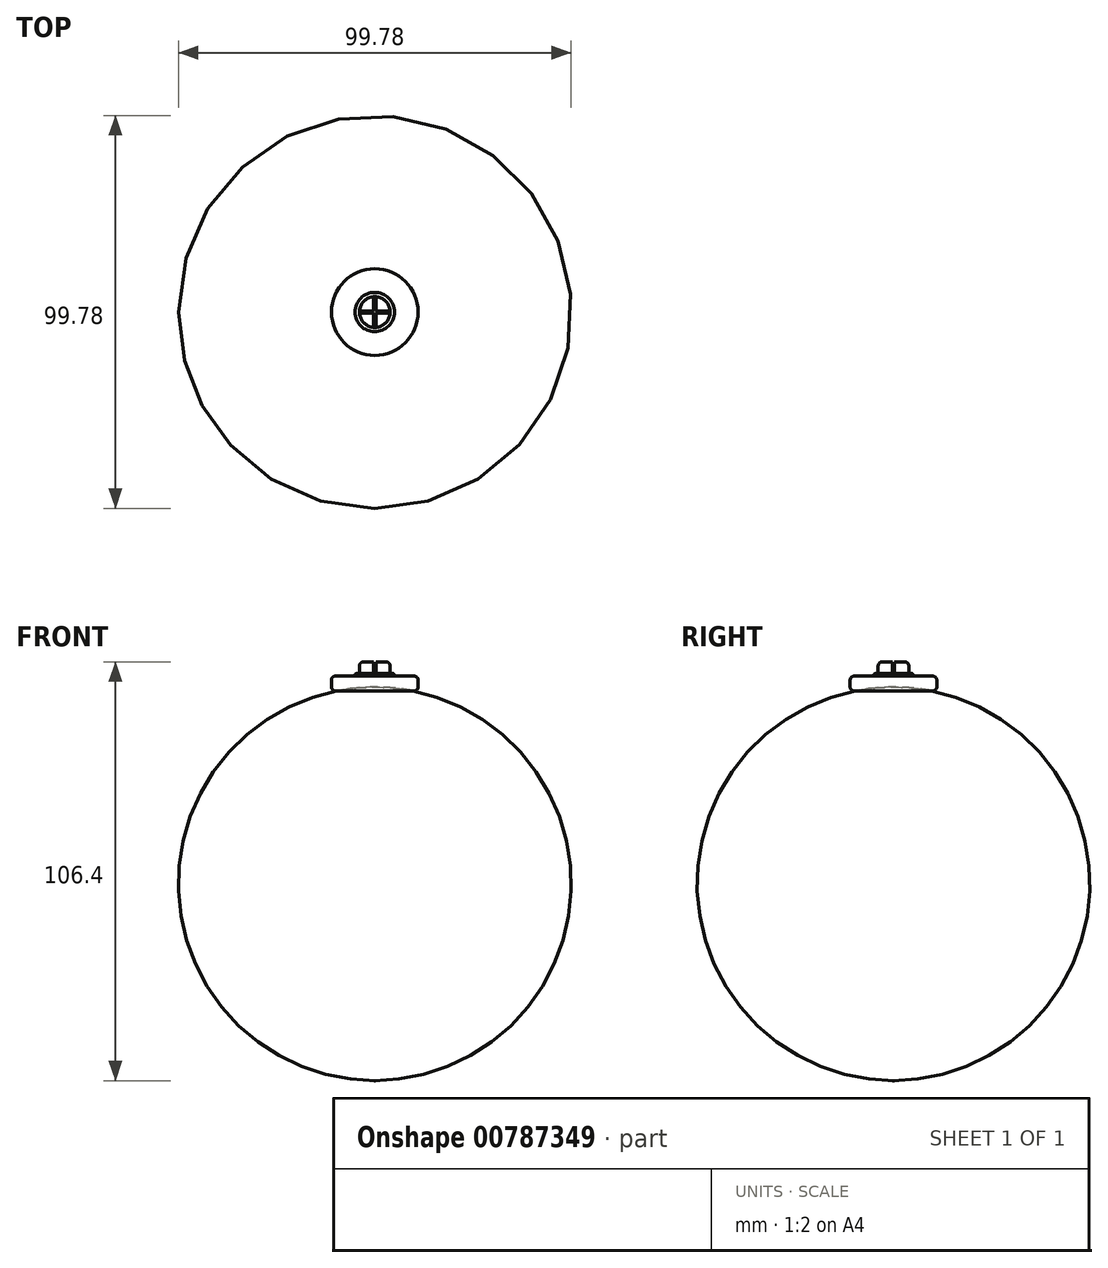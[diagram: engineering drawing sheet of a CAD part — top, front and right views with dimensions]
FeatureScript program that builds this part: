
annotation { "Feature Type Name" : "Feature", "Feature Type Description" : "" }
export const myFeature = defineFeature(function(context is Context, id is Id, definition is map)
    precondition{}
    {
        {
            var Q0;
            Q0=qCreatedBy(makeId("Front.planeOp"),FACE);
            var sketch = newSketch(context, id + "F0", { "sketchPlane" : qUnion([Q0])});
            skLineSegment(sketch, "E0", {"start": v(-11, 0) * mm, "end": v(-11, 4) * mm});
            skLineSegment(sketch, "E1", {"start": v(-11, 4) * mm, "end": v(0, 4) * mm});
            skArc(sketch, "E2", {"start": v(0, 1.2) * mm, "mid": v(-5.53, 0.9) * mm, "end": v(-11, 0) * mm});
            skLineSegment(sketch, "E3", {"start": v(0, 4) * mm, "end": v(0, 1.2) * mm});
            skLineSegment(sketch, "E4", {"start": v(-3.9, 4.6) * mm, "end": v(0, 4.6) * mm});
            skLineSegment(sketch, "E5", {"start": v(0, 4.6) * mm, "end": v(0, 4) * mm});
            skLineSegment(sketch, "E6", {"start": v(-3.9, 4.6) * mm, "end": v(-3.9, 7.6) * mm});
            skLineSegment(sketch, "E7", {"start": v(-3.9, 7.6) * mm, "end": v(0, 7.6) * mm});
            skLineSegment(sketch, "E8", {"start": v(0, 7.6) * mm, "end": v(0, 4.6) * mm});
            skLineSegment(sketch, "E9", {"start": v(-3.9, 4.6) * mm, "end": v(-5, 4.6) * mm});
            skLineSegment(sketch, "E10", {"start": v(-5, 4.6) * mm, "end": v(-5, 4) * mm});
            skSolve(sketch);
        }
        {
            var Q0;
            {var subQ2=sQuery(id+"F0.wireOp",EDGE,"Kpe3LUCm-XfSO-ckMI-Tb2P-7CUM5thwnmXW");Q0=makeQuery(id+"F0.imprint","IMPRINT",FACE,{"disambiguationData":[TD([[makeQuery(id+"F0.imprint","IMPRINT",EDGE,{"derivedFrom":subQ2}),-1.0]])]});}
            var Q1;
            Q1=makeQuery(id+"F0.imprint","IMPRINT",FACE,{"disambiguationData":[TD([[makeQuery(id+"F0.imprint","IMPRINT",EDGE,{"derivedFrom":sQuery(id+"F0.wireOp",EDGE,"E4")}),1.0]])]});
            var Q2;
            {var subQ3=sQuery(id+"F0.wireOp",EDGE,"E0");Q2=makeQuery(id+"F0.imprint","IMPRINT",FACE,{"disambiguationData":[TD([[makeQuery(id+"F0.imprint","IMPRINT",EDGE,{"derivedFrom":subQ3}),-1.0]])]});}
            var Q3;
            Q3=makeQuery(id+"F0.imprint","IMPRINT",FACE,{"disambiguationData":[TD([[makeQuery(id+"F0.imprint","IMPRINT",EDGE,{"derivedFrom":sQuery(id+"F0.wireOp",EDGE,"E4")}),-1.0]])]});
            var Q4;
            Q4=sQuery(id+"F0.wireOp",EDGE,"E8");
            revolve(context, id + "F1", {"surfaceOperationType" : NewSurfaceOperationType.NEW, "entities" : qUnion([Q0, Q1, Q2, Q3]), "axis" : qUnion([Q4]), "revolveType" : RevolveType.FULL});
        }
        {
            var Q0;
            Q0=makeQuery(id+"F1.opRevolve","SWEPT_FACE",FACE,{"disambiguationData":[OSD([sQuery(id+"F0.wireOp",EDGE,"E7")])]});
            var sketch = newSketch(context, id + "F2", { "sketchPlane" : qUnion([Q0])});
            skLineSegment(sketch, "E11", {"start": v(-0.3, 3.89) * mm, "end": v(-0.3, 0.3) * mm});
            skLineSegment(sketch, "E12", {"start": v(-0.3, 0.3) * mm, "end": v(-3.89, 0.3) * mm});
            skLineSegment(sketch, "E13.MirrorCS", {"start": v(0.3, 3.89) * mm, "end": v(0.3, 0.3) * mm});
            skLineSegment(sketch, "E14.MirrorCS", {"start": v(0.3, 0.3) * mm, "end": v(3.89, 0.3) * mm});
            skLineSegment(sketch, "E15.MirrorCS", {"start": v(-0.3, -0.3) * mm, "end": v(-3.89, -0.3) * mm});
            skLineSegment(sketch, "E16.MirrorCS", {"start": v(-0.3, -3.89) * mm, "end": v(-0.3, -0.3) * mm});
            skLineSegment(sketch, "E17.MirrorCS", {"start": v(0.3, -3.89) * mm, "end": v(0.3, -0.3) * mm});
            skLineSegment(sketch, "E18.MirrorCS", {"start": v(0.3, -0.3) * mm, "end": v(3.89, -0.3) * mm});
            skSolve(sketch);
        }
        {
            var Q0;
            {var subQ3=sQuery(id+"F2.wireOp",EDGE,"E11");Q0=makeQuery(id+"F2.imprint","IMPRINT",FACE,{"disambiguationData":[TD([[makeQuery(id+"F2.imprint","IMPRINT",EDGE,{"derivedFrom":subQ3}),1.0]])]});}
            extrude(context, id + "F3", {"entities" : qUnion([Q0]), "operationType" : NewBodyOperationType.REMOVE, "oppositeDirection" : true, "depth" : 2.8 * mm, "offsetDistance" : 25 * mm});
        }
        {
            var Q0;
            Q0=makeQuery(id+"F1.opRevolve","SWEPT_EDGE",EDGE,{"disambiguationData":[OSD([sQuery(id+"F0.wireOp",EDGE,"E0"),sQuery(id+"F0.wireOp",EDGE,"E1")])]});
            var Q1;
            Q1=makeQuery(id+"F1.opRevolve","SWEPT_EDGE",EDGE,{"disambiguationData":[OSD([sQuery(id+"F0.wireOp",EDGE,"E0"),sQuery(id+"F0.wireOp",EDGE,"E2")])]});
            var Q2;
            Q2=makeQuery(id+"F1.opRevolve","SWEPT_EDGE",EDGE,{"disambiguationData":[OSD([sQuery(id+"F0.wireOp",EDGE,"E6"),sQuery(id+"F0.wireOp",EDGE,"E7")])]});
            fillet(context, id + "F4", {"entities" : qUnion([Q0, Q1, Q2]), "radius" : 1 * mm, "tangentPropagation" : true, "allowEdgeOverflow" : false});
        }
        {
            var Q0;
            Q0=makeQuery(id+"F3.boolean.opBoolean","COPY",EDGE,{"derivedFrom":makeQuery(id+"F3.opExtrude","CAP_EDGE",EDGE,{"disambiguationData":[OSD([sQuery(id+"F2.wireOp",EDGE,"E15.MirrorCS")])],"isStart":false})});
            var Q1;
            Q1=makeQuery(id+"F3.boolean.opBoolean","COPY",EDGE,{"derivedFrom":makeQuery(id+"F3.opExtrude","CAP_EDGE",EDGE,{"disambiguationData":[OSD([sQuery(id+"F2.wireOp",EDGE,"E18.MirrorCS")])],"isStart":false})});
            var Q2;
            Q2=makeQuery(id+"F3.boolean.opBoolean","COPY",EDGE,{"derivedFrom":makeQuery(id+"F3.opExtrude","CAP_EDGE",EDGE,{"disambiguationData":[OSD([sQuery(id+"F2.wireOp",EDGE,"E14.MirrorCS")])],"isStart":false})});
            var Q3;
            Q3=makeQuery(id+"F3.boolean.opBoolean","COPY",EDGE,{"derivedFrom":makeQuery(id+"F3.opExtrude","CAP_EDGE",EDGE,{"disambiguationData":[OSD([sQuery(id+"F2.wireOp",EDGE,"E12")])],"isStart":false})});
            var Q4;
            Q4=makeQuery(id+"F3.boolean.opBoolean","COPY",EDGE,{"derivedFrom":makeQuery(id+"F3.opExtrude","SWEPT_EDGE",EDGE,{"disambiguationData":[OSD([sQuery(id+"F2.wireOp",EDGE,"E15.MirrorCS"),sQuery(id+"F2.wireOp",EDGE,"E16.MirrorCS")])]})});
            var Q5;
            Q5=makeQuery(id+"F3.boolean.opBoolean","COPY",EDGE,{"derivedFrom":makeQuery(id+"F3.opExtrude","SWEPT_EDGE",EDGE,{"disambiguationData":[OSD([sQuery(id+"F2.wireOp",EDGE,"E11"),sQuery(id+"F2.wireOp",EDGE,"E12")])]})});
            var Q6;
            Q6=makeQuery(id+"F3.boolean.opBoolean","COPY",EDGE,{"derivedFrom":makeQuery(id+"F3.opExtrude","SWEPT_EDGE",EDGE,{"disambiguationData":[OSD([sQuery(id+"F2.wireOp",EDGE,"E13.MirrorCS"),sQuery(id+"F2.wireOp",EDGE,"E14.MirrorCS")])]})});
            var Q7;
            Q7=makeQuery(id+"F3.boolean.opBoolean","COPY",EDGE,{"derivedFrom":makeQuery(id+"F3.opExtrude","SWEPT_EDGE",EDGE,{"disambiguationData":[OSD([sQuery(id+"F2.wireOp",EDGE,"E17.MirrorCS"),sQuery(id+"F2.wireOp",EDGE,"E18.MirrorCS")])]})});
            var Q8;
            Q8=makeQuery(id+"F3.boolean.opBoolean","COPY",EDGE,{"derivedFrom":makeQuery(id+"F3.opExtrude","CAP_EDGE",EDGE,{"disambiguationData":[OSD([sQuery(id+"F2.wireOp",EDGE,"E17.MirrorCS")])],"isStart":false})});
            var Q9;
            Q9=makeQuery(id+"F3.boolean.opBoolean","COPY",EDGE,{"derivedFrom":makeQuery(id+"F3.opExtrude","CAP_EDGE",EDGE,{"disambiguationData":[OSD([sQuery(id+"F2.wireOp",EDGE,"E13.MirrorCS")])],"isStart":false})});
            var Q10;
            Q10=makeQuery(id+"F3.boolean.opBoolean","COPY",EDGE,{"derivedFrom":makeQuery(id+"F3.opExtrude","CAP_EDGE",EDGE,{"disambiguationData":[OSD([sQuery(id+"F2.wireOp",EDGE,"E11")])],"isStart":false})});
            var Q11;
            Q11=makeQuery(id+"F3.boolean.opBoolean","COPY",EDGE,{"derivedFrom":makeQuery(id+"F3.opExtrude","CAP_EDGE",EDGE,{"disambiguationData":[OSD([sQuery(id+"F2.wireOp",EDGE,"E16.MirrorCS")])],"isStart":false})});
            var Q12;
            Q12=makeQuery(id+"F1.opRevolve","SWEPT_EDGE",EDGE,{"disambiguationData":[OSD([sQuery(id+"F0.wireOp",EDGE,"E9"),sQuery(id+"F0.wireOp",EDGE,"E10")])]});
            fillet(context, id + "F5", {"entities" : qUnion([Q0, Q1, Q2, Q3, Q4, Q5, Q6, Q7, Q8, Q9, Q10, Q11, Q12]), "radius" : .3 * mm, "tangentPropagation" : true, "allowEdgeOverflow" : false});
        }
    });
